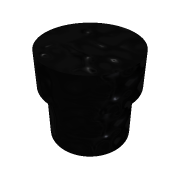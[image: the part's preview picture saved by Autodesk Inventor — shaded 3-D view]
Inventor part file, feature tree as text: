
AUTODESK INVENTOR PART (.ipt)
format: ipt  version: 2019 (Build 230136000, 136)  size: 94,208 bytes
history: native  units: mm
features: revolve x1, sketch x1
ambient origin geometry x8: Origin, YZ Plane, XZ Plane, XY Plane, X Axis, Y Axis, Z Axis, Center Point
bodies: Solid1 (feature_tree)
feature tree (2):
  revolve  "Revolution1"  [1 undecoded]
  sketch  "Sketch1"  dims[d0=11.5mm d1=16.2mm d2=2.4mm d3=10.6mm d4=90.0deg]
note: 1 required parameter value undecoded (feature->parameter linkage not recoverable at this tier; creation-order binding heuristic only, values carry confidence <= 0.55)
